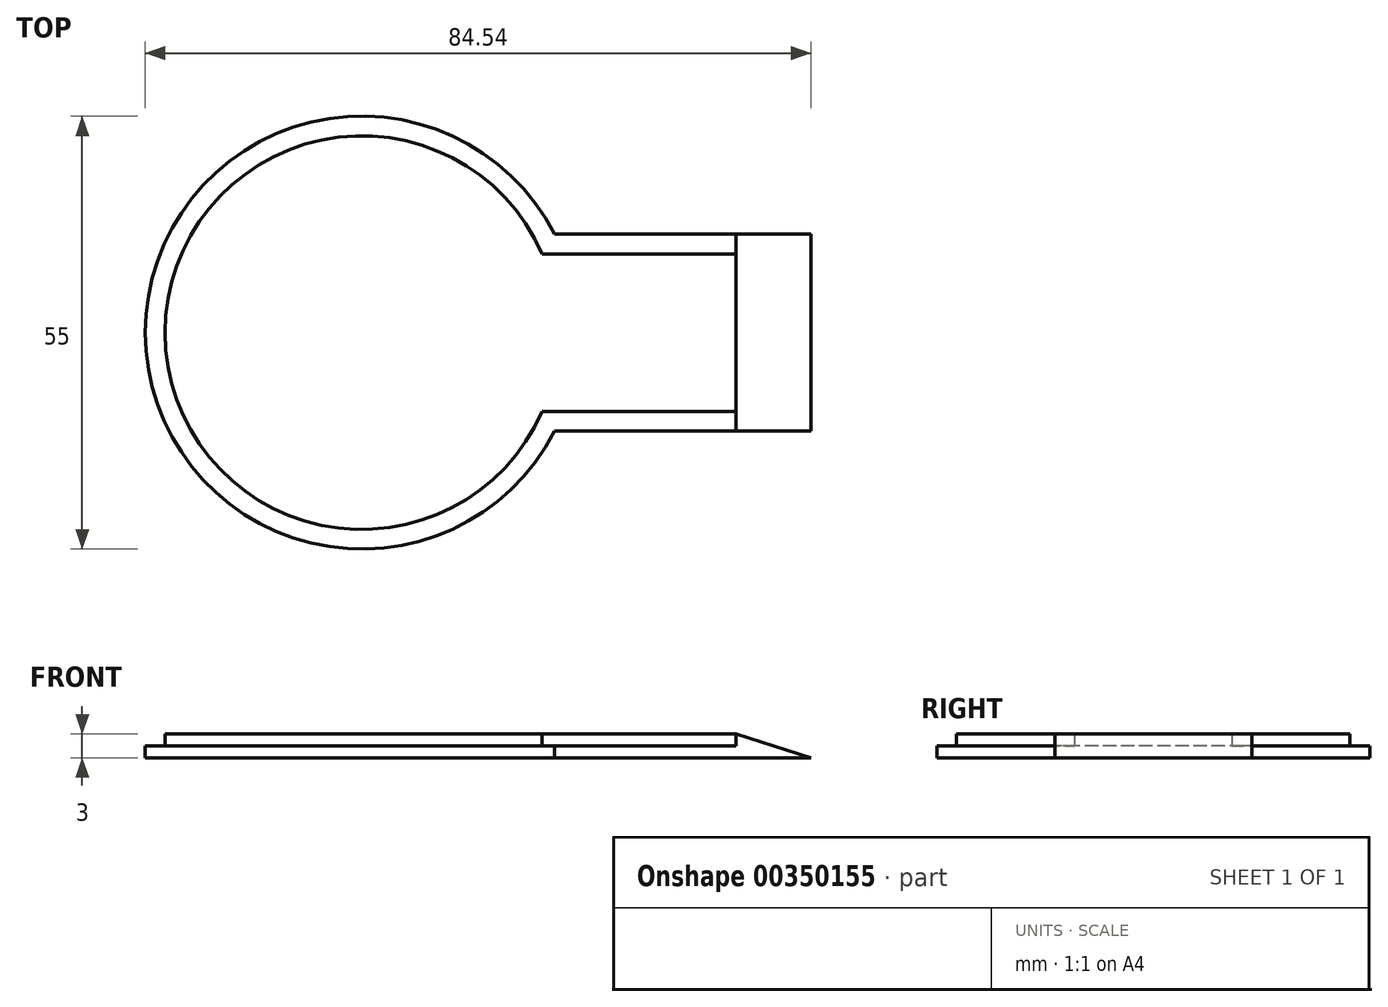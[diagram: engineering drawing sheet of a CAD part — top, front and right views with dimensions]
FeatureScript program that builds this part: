
annotation { "Feature Type Name" : "Feature", "Feature Type Description" : "" }
export const myFeature = defineFeature(function(context is Context, id is Id, definition is map)
    precondition{}
    {
        {
            var Q0;
            Q0=qCreatedBy(makeId("Top.planeOp"),FACE);
            var sketch = newSketch(context, id + "F0", { "sketchPlane" : qUnion([Q0])});
            skLineSegment(sketch, "E0.bottom", {"start": v(27.5, 10) * mm, "end": v(47.5, 10) * mm});
            skLineSegment(sketch, "E0.top", {"start": v(27.5, -10) * mm, "end": v(47.5, -10) * mm});
            skLineSegment(sketch, "E0.left", {"start": v(27.5, 10) * mm, "end": v(27.5, -10) * mm});
            skLineSegment(sketch, "E0.right", {"start": v(47.5, 10) * mm, "end": v(47.5, -10) * mm});
            skLineSegment(sketch, "E1", {"start": v(27.5, 10) * mm, "end": v(22.91, 10) * mm});
            skLineSegment(sketch, "E2", {"start": v(27.5, -10) * mm, "end": v(22.91, -10) * mm});
            skLineSegment(sketch, "E3.bottom", {"start": v(27.5, 12.5) * mm, "end": v(47.5, 12.5) * mm});
            skLineSegment(sketch, "E3.top", {"start": v(27.5, -12.5) * mm, "end": v(47.5, -12.5) * mm});
            skLineSegment(sketch, "E3.left", {"start": v(27.5, 12.5) * mm, "end": v(27.5, -12.5) * mm, "construction": true});
            skLineSegment(sketch, "E3.right", {"start": v(47.5, 12.5) * mm, "end": v(47.5, -12.5) * mm});
            skLineSegment(sketch, "E4", {"start": v(0, 0) * mm, "end": v(27.5, 0) * mm, "construction": true});
            skPoint(sketch, "E4.endSnap0", {"position": v(27.5, 0) * mm});
            skPoint(sketch, "E5.startSnap0", {"position": v(47.5, 0) * mm});
            skLineSegment(sketch, "E6", {"start": v(27.5, 12.5) * mm, "end": v(24.5, 12.5) * mm});
            skLineSegment(sketch, "E7", {"start": v(24.5, -12.5) * mm, "end": v(27.5, -12.5) * mm});
            skLineSegment(sketch, "E8", {"start": v(22.91, 10) * mm, "end": v(22.91, 10) * mm});
            skArc(sketch, "E9", {"start": v(22.91, -10) * mm, "mid": v(25, 0) * mm, "end": v(22.91, 10) * mm, "construction": true});
            skArc(sketch, "E10", {"start": v(22.91, 10) * mm, "mid": v(-25, 0) * mm, "end": v(22.91, -10) * mm});
            skLineSegment(sketch, "E11", {"start": v(24.5, 12.5) * mm, "end": v(24.5, 12.5) * mm});
            skArc(sketch, "E12", {"start": v(24.5, -12.5) * mm, "mid": v(27.5, 0) * mm, "end": v(24.5, 12.5) * mm, "construction": true});
            skArc(sketch, "E13", {"start": v(24.5, 12.5) * mm, "mid": v(-27.5, 0) * mm, "end": v(24.5, -12.5) * mm});
            skSolve(sketch);
        }
        {
            var Q0;
            {var subQ3=sQuery(id+"F0.wireOp",EDGE,"E0.bottom");Q0=makeQuery(id+"F0.imprint","IMPRINT",FACE,{"disambiguationData":[TD([[makeQuery(id+"F0.imprint","IMPRINT",EDGE,{"derivedFrom":subQ3}),1.0]])]});}
            extrude(context, id + "F1", {"entities" : qUnion([Q0]), "depth" : 1.5 * mm});
        }
        {
            var Q0;
            Q0=makeQuery(id+"F0.imprint","IMPRINT",FACE,{"disambiguationData":[TD([[makeQuery(id+"F0.imprint","IMPRINT",EDGE,{"derivedFrom":sQuery(id+"F0.wireOp",EDGE,"E0.left")}),-1.0]])]});
            var Q1;
            {var subQ0=sQuery(id+"F0.wireOp",EDGE,"E0.bottom");Q1=makeQuery(id+"F0.imprint","IMPRINT",FACE,{"disambiguationData":[TD([[makeQuery(id+"F0.imprint","IMPRINT",EDGE,{"derivedFrom":subQ0}),-1.0]])]});}
            extrude(context, id + "F2", {"entities" : qUnion([Q0, Q1]), "operationType" : NewBodyOperationType.ADD, "depth" : 3 * mm});
        }
        {
            var Q0;
            Q0=qCreatedBy(makeId("Front.planeOp"),FACE);
            var sketch = newSketch(context, id + "F3", { "sketchPlane" : qUnion([Q0])});
            skLineSegment(sketch, "E14", {"start": v(47.5, 0) * mm, "end": v(47.5, 3) * mm});
            skLineSegment(sketch, "E15", {"start": v(47.5, 3) * mm, "end": v(57.04, 0) * mm});
            skLineSegment(sketch, "E16", {"start": v(57.04, 0) * mm, "end": v(47.5, 0) * mm});
            skSolve(sketch);
        }
        {
            var Q0;
            Q0=makeQuery(id+"F3.imprint","IMPRINT",FACE,{"disambiguationData":[TD([[makeQuery(id+"F3.imprint","IMPRINT",EDGE,{"derivedFrom":sQuery(id+"F3.wireOp",EDGE,"E14")}),-1.0]])]});
            extrude(context, id + "F4", {"entities" : qUnion([Q0]), "operationType" : NewBodyOperationType.ADD, "endBound" : BoundingType.SYMMETRIC, "depth" : 25 * mm});
        }
    });
